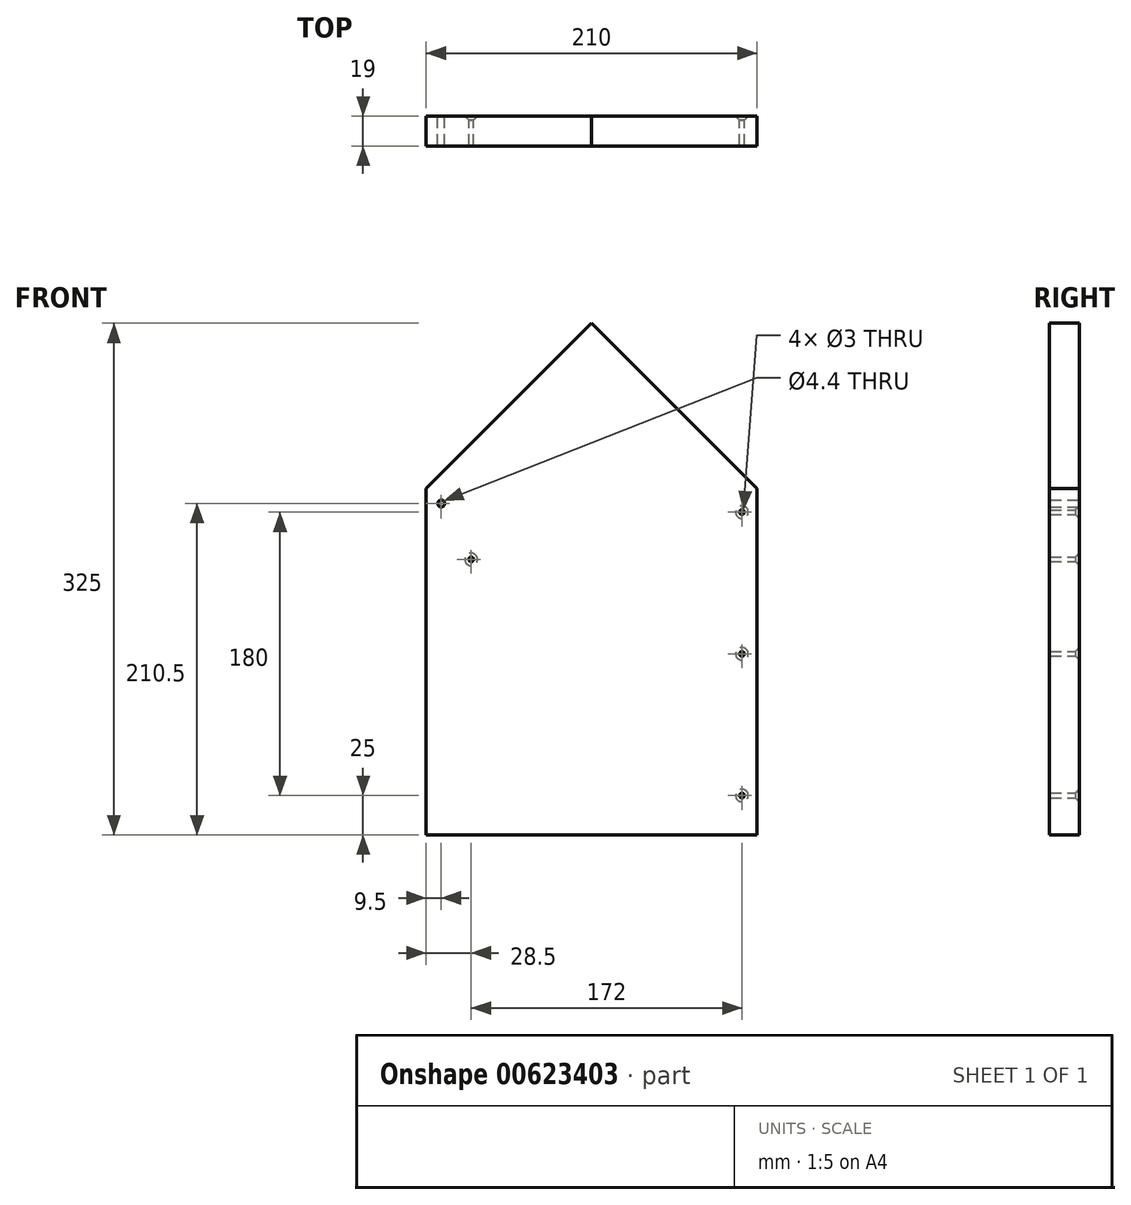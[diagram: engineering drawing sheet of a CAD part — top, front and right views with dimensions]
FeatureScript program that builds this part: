
annotation { "Feature Type Name" : "Feature", "Feature Type Description" : "" }
export const myFeature = defineFeature(function(context is Context, id is Id, definition is map)
    precondition{}
    {
        {
            var Q0;
            Q0=qCreatedBy(makeId("Front.planeOp"),FACE);
            var sketch = newSketch(context, id + "F0", { "sketchPlane" : qUnion([Q0])});
            skLineSegment(sketch, "E0", {"start": v(105, 0) * mm, "end": v(105, 220) * mm});
            skLineSegment(sketch, "E1", {"start": v(105, 220) * mm, "end": v(0, 325) * mm});
            skLineSegment(sketch, "E2.MirrorCS", {"start": v(-105, 220) * mm, "end": v(0, 325) * mm});
            skLineSegment(sketch, "E3.MirrorCS", {"start": v(-105, 0) * mm, "end": v(-105, 220) * mm});
            skLineSegment(sketch, "E4", {"start": v(-105, 0) * mm, "end": v(105, 0) * mm});
            skSolve(sketch);
        }
        {
            var Q0;
            Q0 = qSketchRegion(id + "F0", true);
            extrude(context, id + "F1", {"entities" : qUnion([Q0]), "depth" : -19 * mm, "offsetDistance" : 25 * mm});
        }
        {
            var Q0;
            Q0=makeQuery(id+"F1.opExtrude","CAP_FACE",FACE,{"disambiguationData":[OSD([sQuery(id+"F0.wireOp",EDGE,"E0"),sQuery(id+"F0.wireOp",EDGE,"E1"),sQuery(id+"F0.wireOp",EDGE,"E2.MirrorCS"),sQuery(id+"F0.wireOp",EDGE,"E3.MirrorCS"),sQuery(id+"F0.wireOp",EDGE,"E4")])],"isStart":false});
            var sketch = newSketch(context, id + "F2", { "sketchPlane" : qUnion([Q0])});
            skPoint(sketch, "E5", {"position": v(-95.5, 25) * mm});
            skPoint(sketch, "E6", {"position": v(-95.5, 205) * mm});
            skPoint(sketch, "E7", {"position": v(95.5, 210.5) * mm});
            skPoint(sketch, "E8", {"position": v(-95.5, 115) * mm});
            skLineSegment(sketch, "E9", {"start": v(-95.5, 205) * mm, "end": v(-95.5, 115) * mm, "construction": true});
            skLineSegment(sketch, "E10", {"start": v(-95.5, 115) * mm, "end": v(-95.5, 25) * mm, "construction": true});
            skPoint(sketch, "E11", {"position": v(76.5, 175) * mm});
            skSolve(sketch);
        }
        {
            var Q0;
            Q0=sQuery(id+"F2.wireOp",VERTEX,"E5");
            var Q1;
            Q1=sQuery(id+"F2.wireOp",VERTEX,"E8");
            var Q2;
            Q2=sQuery(id+"F2.wireOp",VERTEX,"E6");
            var Q3;
            Q3=sQuery(id+"F2.wireOp",VERTEX,"E11");
            var Q4;
            Q4=makeQuery(id+"F1.opExtrude","SWEPT_BODY",BODY,{"disambiguationData":[OSD([sQuery(id+"F0.wireOp",EDGE,"E0"),sQuery(id+"F0.wireOp",EDGE,"E1"),sQuery(id+"F0.wireOp",EDGE,"E2.MirrorCS"),sQuery(id+"F0.wireOp",EDGE,"E3.MirrorCS"),sQuery(id+"F0.wireOp",EDGE,"E4")])]});
            hole(context, id + "F3", {"style" : HoleStyle.C_SINK, "endStyle" : HoleEndStyle.THROUGH, "holeDiameter" : 3 * mm, "cSinkDiameter" : 8 * mm, "cSinkAngle" : 90 * degree, "majorDiameter" : 5 * mm, "isTappedThrough" : true, "tappedDepth" : 12 * mm, "tapClearance" : 3, "startFromSketch" : true, "locations" : qUnion([Q0, Q1, Q2, Q3]), "scope" : qUnion([Q4])});
        }
        {
            var Q0;
            Q0=sQuery(id+"F2.wireOp",VERTEX,"E7");
            var Q1;
            Q1=makeQuery(id+"F1.opExtrude","SWEPT_BODY",BODY,{"disambiguationData":[OSD([sQuery(id+"F0.wireOp",EDGE,"E0"),sQuery(id+"F0.wireOp",EDGE,"E1"),sQuery(id+"F0.wireOp",EDGE,"E2.MirrorCS"),sQuery(id+"F0.wireOp",EDGE,"E3.MirrorCS"),sQuery(id+"F0.wireOp",EDGE,"E4")])]});
            hole(context, id + "F4", {"style" : HoleStyle.SIMPLE, "endStyle" : HoleEndStyle.THROUGH, "standardTappedOrClearance" : lookupTablePath({ "standard" : "ISO", "fit" : "Normal", "size" : "M4", "type" : "Clearance" }), "standardBlindInLast" : lookupTablePath({ "fit" : "Standard", "standard" : "ISO", "size" : "M4", "type" : "Clearance" }), "holeDiameter" : 4.4 * mm, "majorDiameter" : 5 * mm, "isTappedThrough" : true, "tappedDepth" : 12 * mm, "tapClearance" : 3, "startFromSketch" : true, "locations" : qUnion([Q0]), "scope" : qUnion([Q1])});
        }
    });
